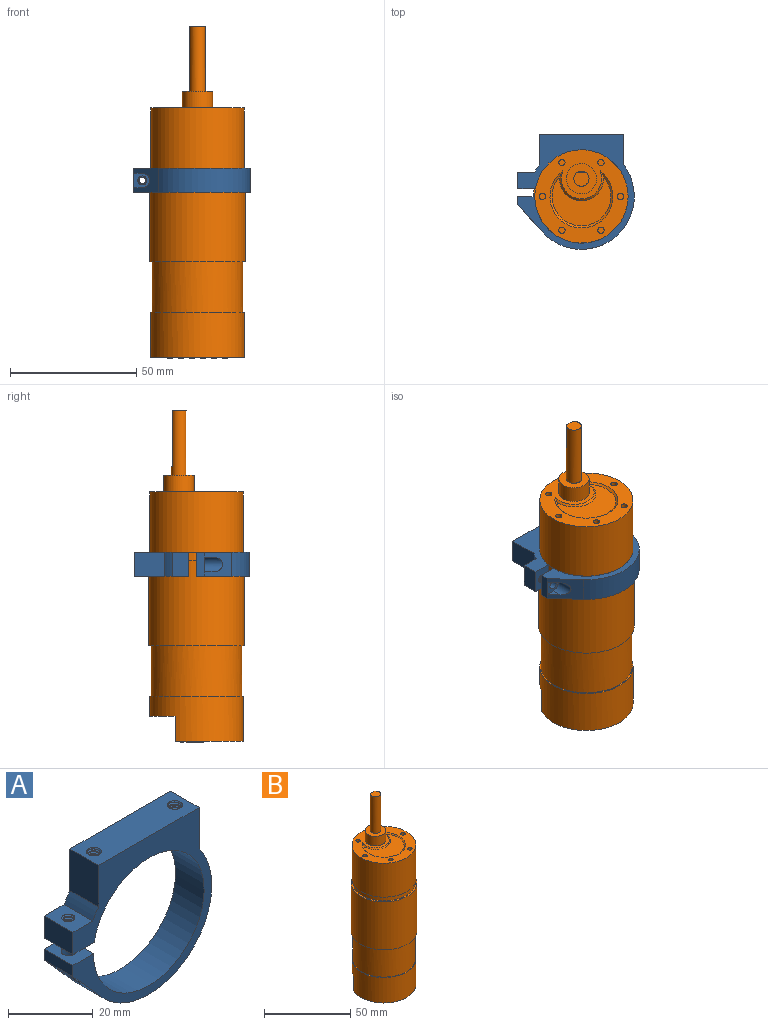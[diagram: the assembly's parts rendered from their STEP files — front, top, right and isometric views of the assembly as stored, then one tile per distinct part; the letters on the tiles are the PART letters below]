
ASSEMBLY  parts=2 mates=1
PART A: 53 faces, bbox 46.4x9.7x45.9 mm
  f0: cylinder r=1.75mm len=6.54mm, axis (0,0,-1), area 9mm2, adj f34,f50,f51,f52
  f1: cylinder r=1.75mm len=6.54mm, axis (0,0,-1), area 9mm2, adj f34,f47,f48,f49
  f2: cylinder r=1.75mm len=6.35mm, axis (0,0,1), area 8.7mm2, adj f30,f31,f45,f46
  f3: cylinder r=1.35mm len=6.35mm, axis (0,0,-1), area 15.8mm2, adj f30,f31,f45,f46
  f4: cylinder r=1.78mm len=3.56mm, axis (0,0,-1), area 35.5mm2, adj f38,f44
  f5: cylinder r=2.92mm len=7.1mm, axis (0,0,1), area 54.3mm2, adj f36,f42,f43,f44
  f6: cylinder r=1.35mm len=2.71mm, axis (0,0,1), area 7.6mm2, adj f7,f15,f47,f48,f49
  f7: cylinder r=1.35mm len=2.71mm, axis (0,0,1), area 2mm2, adj f6,f8,f48,f49
  f8: cylinder r=1.35mm len=2.71mm, axis (0,0,1), area 2mm2, adj f7,f9,f48,f49
  f9: cylinder r=1.35mm len=2.71mm, axis (0,0,1), area 2mm2, adj f8,f10,f48,f49
  f10: cylinder r=1.35mm len=2.71mm, axis (0,0,1), area 2mm2, adj f9,f11,f48,f49
  f11: cylinder r=1.35mm len=2.71mm, axis (0,0,1), area 2mm2, adj f10,f12,f48,f49
  f12: cylinder r=1.35mm len=2.71mm, axis (0,0,1), area 2mm2, adj f11,f13,f48,f49
  f13: cylinder r=1.35mm len=2.71mm, axis (0,0,1), area 2mm2, adj f12,f14,f48,f49
  f14: cylinder r=1.35mm len=2.71mm, axis (0,0,1), area 1.3mm2, adj f13,f28,f48,f49
  f15: cone r=1.35mm half-angle=59deg, axis (0,0,1), area 6.7mm2, adj f6
  f16: cylinder r=1.35mm len=2.71mm, axis (0,0,1), area 7.6mm2, adj f17,f25,f50,f51,f52
  f17: cylinder r=1.35mm len=2.71mm, axis (0,0,1), area 2mm2, adj f16,f18,f51,f52
  f18: cylinder r=1.35mm len=2.71mm, axis (0,0,1), area 2mm2, adj f17,f19,f51,f52
  f19: cylinder r=1.35mm len=2.71mm, axis (0,0,1), area 2mm2, adj f18,f20,f51,f52
  f20: cylinder r=1.35mm len=2.71mm, axis (0,0,1), area 2mm2, adj f19,f21,f51,f52
  f21: cylinder r=1.35mm len=2.71mm, axis (0,0,1), area 2mm2, adj f20,f22,f51,f52
  f22: cylinder r=1.35mm len=2.71mm, axis (0,0,1), area 2mm2, adj f21,f23,f51,f52
  f23: cylinder r=1.35mm len=2.71mm, axis (0,0,1), area 2mm2, adj f22,f24,f51,f52
  f24: cylinder r=1.35mm len=2.71mm, axis (0,0,1), area 1.3mm2, adj f23,f29,f51,f52
  f25: cone r=1.35mm half-angle=59deg, axis (0,0,1), area 6.7mm2, adj f16
  f26: cylinder r=18.41mm len=36.83mm, axis (0,-1,0), area 1071.7mm2, adj f30,f38,f40,f41
  f27: cylinder r=20.96mm len=36.58mm, axis (0,-1,0), area 610.3mm2, adj f35,f36,f40,f41
  f28: cone r=1.35mm half-angle=45deg, axis (0,0,1), area 3.3mm2, adj f14,f34,f48,f49
  f29: cone r=1.35mm half-angle=45deg, axis (0,0,1), area 3.3mm2, adj f24,f34,f51,f52
  f30: plane 9.72x7.33mm, normal (0,0,-1), area 60.6mm2, adj f2,f3,f26,f39,f40,f41,f45,f46
  f31: plane 9.72x6.8mm, normal (0,0,1), area 55.6mm2, adj f2,f3,f32,f39,f40,f41,f45,f46
  f32: cylinder r=20.96mm len=9.53mm, axis (0,-1,0), area 34.7mm2, adj f31,f33,f40,f41
  f33: plane 11.96x9.53mm, normal (-1,0,0), area 113.9mm2, adj f32,f34,f40,f41
  f34: plane 33.48x9.53mm, normal (0,0,1), area 299.6mm2, adj f0,f1,f28,f29,f33,f35,f40,f41
  f35: plane 11.96x9.53mm, normal (1,0,0), area 113.9mm2, adj f27,f34,f40,f41
  f36: plane 10.79x9.65mm, normal (-0.75,0,-0.67), area 87.8mm2, adj f5,f27,f37,f40,f41,f42,f43
  f37: plane 9.53x3.18mm, normal (-1,0,0), area 30.2mm2, adj f36,f38,f40,f41,f44
  f38: plane 9.53x6.86mm, normal (0,0,1), area 55.4mm2, adj f4,f26,f37,f40,f41
  f39: plane 9.53x6.35mm, normal (-1,0,0), area 60.5mm2, adj f30,f31,f40,f41
  f40: plane 46.23x45.52mm, normal (0,1,0), area 576.9mm2, adj f26,f27,f30,f31,f32,f33,f34,f35
  f41: plane 46.23x45.52mm, normal (0,-1,0), area 576.9mm2, adj f26,f27,f30,f31,f32,f33,f34,f35
  f42: plane 3.83x3.43mm, normal (0,-1,0), area 6.6mm2, adj f5,f36,f44
  f43: plane 3.83x3.43mm, normal (0,1,0), area 6.6mm2, adj f5,f36,f44
  f44: plane 6.35x5.84mm, normal (0,0,-1), area 23.5mm2, adj f4,f5,f37,f42,f43
  f45: bspline ~6.87x3.95mm, area 36.1mm2, adj f2,f3,f30,f31
  f46: bspline ~6.81x3.5mm, area 36.1mm2, adj f2,f3,f30,f31
  f47: cone r=0.98mm half-angle=55deg, axis (0,0,1), area 1.9mm2, adj f1,f6,f48,f49
  f48: bspline ~7.28x3.49mm, area 36.9mm2, adj f1,f6,f7,f8,f9,f10,f11,f12
  f49: bspline ~6.82x3.5mm, area 36.9mm2, adj f1,f6,f7,f8,f9,f10,f11,f12
  f50: cone r=0.98mm half-angle=55deg, axis (0,0,1), area 1.9mm2, adj f0,f16,f51,f52
  f51: bspline ~7.28x3.49mm, area 36.9mm2, adj f0,f16,f17,f18,f19,f20,f21,f22
  f52: bspline ~6.82x3.5mm, area 36.9mm2, adj f0,f16,f17,f18,f19,f20,f21,f22
PART B: 327 faces, bbox 38x38x131.7 mm
  f0: cone r=12.5mm half-angle=50deg, axis (0,0,1), area 63.4mm2, adj f1,f13,f284
  f1: cone r=8mm half-angle=45deg, axis (0,0,-1), area 30mm2, adj f0,f13,f284
  f2: plane 37x27mm, normal (0,0,-1), area 818.4mm2, adj f8,f14,f15,f16,f17,f18,f19,f20
  f3: plane 12x12mm, normal (0,0,1), area 84.8mm2, adj f10,f201
  f4: cylinder r=18.5mm len=37mm, axis (0,0,1), area 2789.7mm2, adj f253,f284
  f5: plane 0.87x0.8mm, normal (0,0,-1), area 0.5mm2, adj f32,f133,f223,f224
  f6: plane 0.87x0.8mm, normal (0,0,-1), area 0.5mm2, adj f244,f245,f246,f247
  f7: cylinder r=18mm len=36mm, axis (0,0,-1), area 2261.9mm2, adj f12,f70
  f8: cylinder r=18.5mm len=37mm, axis (0,0,-1), area 1687.7mm2, adj f2,f55,f70,f278
  f9: cylinder r=18mm len=36mm, axis (0,0,-1), area 339.3mm2, adj f11,f253
  f10: cylinder r=6mm len=12mm, axis (0,0,1), area 252.6mm2, adj f3,f284
  f11: plane 38x38mm, normal (0,0,1), area 116.2mm2, adj f9,f265
  f12: plane 38x38mm, normal (0,0,-1), area 116.2mm2, adj f7,f265
  f13: plane 23.33x19.48mm, normal (0,0,1), area 248.3mm2, adj f0,f1
  f14: plane 0.93x0.2mm, normal (-1,0,0), area 0.2mm2, adj f2,f152,f153,f216
  f15: bspline ~0.48x0.44mm, area 0.1mm2, adj f2,f130,f290,f324
  f16: bspline ~0.8x0.62mm, area 0.2mm2, adj f2,f203,f297,f300
  f17: plane 0.21x0.2mm, normal (0,-1,0), area 0mm2, adj f2,f72,f130,f316
  f18: bspline ~0.87x0.42mm, area 0.2mm2, adj f2,f75,f109,f256
  f19: plane 0.2x0.18mm, normal (1,0,0), area 0mm2, adj f2,f50,f206,f310
  f20: bspline ~0.71x0.33mm, area 0.2mm2, adj f2,f75,f256,f322
  f21: plane 0.2x0.18mm, normal (-1,0,0), area 0mm2, adj f2,f137,f205,f280
  f22: bspline ~0.61x0.56mm, area 0.2mm2, adj f2,f45,f130,f255
  f23: plane 1.57x1.32mm, normal (0.64,0.77,0), area 0.4mm2, adj f2,f98,f204,f280
  f24: bspline ~0.28x0.2mm, area 0.1mm2, adj f2,f105,f178,f179
  f25: plane 0.87x0.6mm, normal (0.57,-0.82,0), area 0.2mm2, adj f53,f200,f270,f279
  f26: plane 0.2x0.15mm, normal (0.73,-0.69,0), area 0mm2, adj f2,f132,f203,f319
  f27: plane 0.53x0.2mm, normal (0,-1,0), area 0.1mm2, adj f2,f96,f232,f325
  f28: bspline ~0.6x0.51mm, area 0.2mm2, adj f2,f58,f105,f184
  f29: bspline ~0.33x0.2mm, area 0.1mm2, adj f2,f60,f149,f303
  f30: bspline ~0.7x0.7mm, area 0.2mm2, adj f2,f104,f121,f294
  f31: plane 0.2x0.16mm, normal (0.79,-0.61,0), area 0mm2, adj f2,f40,f118,f191
  f32: bspline ~0.45x0.4mm, area 0.1mm2, adj f5,f133,f223,f326
  f33: plane 0.2x0.16mm, normal (0.79,-0.61,0), area 0mm2, adj f2,f225,f256,f262
  f34: plane 1.44x0.72mm, normal (0.45,0.89,0), area 0.3mm2, adj f2,f207,f208,f212
  f35: bspline ~0.83x0.35mm, area 0.2mm2, adj f2,f36,f37,f199
  f36: bspline ~0.87x0.42mm, area 0.2mm2, adj f2,f35,f196,f199
  f37: bspline ~0.71x0.25mm, area 0.2mm2, adj f2,f35,f39,f199
  f38: bspline ~0.87x0.42mm, area 0.2mm2, adj f2,f39,f198,f199
  f39: bspline ~1.08x1.04mm, area 0.3mm2, adj f2,f37,f38,f199
  f40: plane 2.1x1.95mm, normal (0,0,-1), area 1mm2, adj f31,f65,f118,f122,f125,f126,f191,f192
  f41: plane 1.44x0.72mm, normal (0.45,-0.89,0), area 0.3mm2, adj f2,f128,f208,f212
  f42: plane 0.23x0.2mm, normal (-1,0,0), area 0mm2, adj f129,f251,f254,f283
  f43: plane 0.2x0.03mm, normal (-1,0,0), area 0mm2, adj f2,f94,f160,f164
  f44: bspline ~0.63x0.2mm, area 0.1mm2, adj f2,f92,f283,f313
  f45: plane 0.2x0.18mm, normal (-1,0,0), area 0mm2, adj f2,f22,f130,f146
  f46: plane 0.37x0.2mm, normal (-1,0,0), area 0.1mm2, adj f2,f50,f95,f206
  f47: bspline ~0.61x0.61mm, area 0.2mm2, adj f2,f218,f219,f326
  f48: bspline ~0.59x0.59mm, area 0.2mm2, adj f2,f219,f220,f326
  f49: plane 2.5x2.5mm, normal (0,0,1), area 4.9mm2, adj f257
  f50: plane 2x0.2mm, normal (0,-1,0), area 0.4mm2, adj f2,f19,f46,f206
  f51: bspline ~0.43x0.41mm, area 0.1mm2, adj f2,f153,f214,f215
  f52: plane 1.36x0.2mm, normal (1,0,0), area 0.3mm2, adj f2,f90,f153,f216
  f53: plane 0.6x0.2mm, normal (-1,0,0), area 0.1mm2, adj f25,f200,f270,f279
  f54: plane 0.21x0.2mm, normal (0,1,0), area 0mm2, adj f2,f100,f147,f213
  f55: plane 32.86x10mm, normal (0,0,-1), area 234.6mm2, adj f8,f278
  f56: bspline ~0.2x0.17mm, area 0.1mm2, adj f2,f106,f271,f299
  f57: plane 2x0.27mm, normal (-0.13,-0.99,0), area 0.4mm2, adj f2,f135,f209,f212
  f58: bspline ~0.58x0.52mm, area 0.2mm2, adj f2,f28,f105,f183
  f59: bspline ~0.24x0.2mm, area 0mm2, adj f2,f104,f121,f304
  f60: plane 2.05x1.28mm, normal (0,0,-1), area 0.8mm2, adj f29,f82,f83,f85,f86,f87,f108,f142
  f61: plane 2x0.26mm, normal (-0.13,0.99,0), area 0.4mm2, adj f2,f79,f131,f212
  f62: plane 0.2x0.18mm, normal (1,0,0), area 0mm2, adj f2,f99,f153,f214
  f63: plane 0.62x0.2mm, normal (1,0,0), area 0.1mm2, adj f2,f103,f258,f283
  f64: bspline ~0.2x0.17mm, area 0.1mm2, adj f2,f233,f235,f236
  f65: plane 0.2x0.16mm, normal (-0.8,-0.6,0), area 0mm2, adj f2,f40,f125,f193
  f66: plane 0.31x0.2mm, normal (1,0,0), area 0.1mm2, adj f2,f95,f206,f310
  f67: plane 1.59x1.09mm, normal (-0.57,0.82,0), area 0.4mm2, adj f2,f143,f200,f291
  f68: bspline ~0.89x0.84mm, area 0.3mm2, adj f2,f203,f297,f319
  f69: plane 0.2x0.04mm, normal (-1,0,0), area 0mm2, adj f2,f145,f280,f315
  f70: plane 37x37mm, normal (0,0,1), area 57.3mm2, adj f7,f8
  f71: plane 1x0.21mm, normal (-0.2,0.98,0), area 0.2mm2, adj f2,f121,f287,f298
  f72: plane 0.82x0.2mm, normal (-1,0,0), area 0.2mm2, adj f2,f17,f130,f308
  f73: plane 2.1x1.23mm, normal (0,0,-1), area 0.8mm2, adj f127,f237,f238,f239,f240,f241,f242,f243
  f74: bspline ~0.51x0.42mm, area 0.1mm2, adj f2,f105,f177,f178
  f75: plane 0.2x0.16mm, normal (-0.8,-0.6,0), area 0mm2, adj f2,f18,f20,f256
  f76: bspline ~0.73x0.33mm, area 0.2mm2, adj f2,f148,f198,f199
  f77: plane 0.69x0.2mm, normal (0,1,0), area 0.1mm2, adj f2,f227,f232,f286
  f78: plane 0.2x0.18mm, normal (1,0,0), area 0mm2, adj f2,f159,f160,f164
  f79: plane 0.2x0.03mm, normal (-1,0,0), area 0mm2, adj f2,f61,f211,f212
  f80: plane 0.2x0.18mm, normal (1,0,0), area 0mm2, adj f2,f204,f280,f315
  f81: plane 0.53x0.2mm, normal (0.2,-0.98,0), area 0.1mm2, adj f2,f117,f130,f316
  f82: plane 2.05x0.2mm, normal (0,1,0), area 0.4mm2, adj f2,f60,f83,f86
  f83: plane 0.2x0.18mm, normal (1,0,0), area 0mm2, adj f2,f60,f82,f275
  f84: plane 2.1x1.95mm, normal (0,0,-1), area 1mm2, adj f91,f107,f120,f139,f141,f259,f261,f266
  f85: plane 0.87x0.2mm, normal (0,-1,0), area 0.2mm2, adj f2,f60,f86,f87
  f86: plane 0.2x0.18mm, normal (-1,0,0), area 0mm2, adj f2,f60,f82,f85
  f87: bspline ~0.56x0.3mm, area 0.1mm2, adj f2,f60,f85,f295
  f88: bspline ~0.71x0.33mm, area 0.2mm2, adj f2,f196,f197,f199
  f89: plane 0.2x0.03mm, normal (1,0,0), area 0mm2, adj f2,f185,f186,f190
  f90: plane 0.83x0.78mm, normal (-0.68,0.73,0), area 0.2mm2, adj f2,f52,f153,f215
  f91: bspline ~0.73x0.33mm, area 0.2mm2, adj f2,f84,f139,f281
  f92: bspline ~0.95x0.6mm, area 0.2mm2, adj f2,f44,f258,f283
  f93: bspline ~0.65x0.63mm, area 0.2mm2, adj f2,f117,f130,f255
  f94: plane 1.64x0.82mm, normal (-0.45,0.89,0), area 0.4mm2, adj f2,f43,f161,f164
  f95: plane 0.21x0.2mm, normal (-0.5,0.87,0), area 0mm2, adj f2,f46,f66,f206
  f96: plane 0.2x0.18mm, normal (1,0,0), area 0mm2, adj f2,f27,f97,f232
  f97: plane 2.05x0.2mm, normal (0,1,0), area 0.4mm2, adj f2,f96,f231,f232
  f98: plane 0.2x0.04mm, normal (1,0,0), area 0mm2, adj f2,f23,f205,f280
  f99: bspline ~0.67x0.65mm, area 0.2mm2, adj f2,f62,f151,f153
  f100: plane 0.77x0.2mm, normal (1,0,0), area 0.2mm2, adj f2,f54,f124,f147
  f101: plane 22.23x3.32mm, normal (0,1,0), area 73.7mm2, adj f201,f248,f289
  f102: plane 0.21x0.2mm, normal (0,1,0), area 0mm2, adj f2,f203,f296,f300
  f103: plane 2x0.2mm, normal (0,1,0), area 0.4mm2, adj f2,f63,f283,f313
  f104: bspline ~0.65x0.63mm, area 0.2mm2, adj f2,f30,f59,f121
  f105: plane 2.1x1.36mm, normal (0,0,-1), area 0.9mm2, adj f24,f28,f58,f74,f113,f114,f115,f175
  f106: bspline ~0.2x0.17mm, area 0.1mm2, adj f2,f56,f292,f299
  f107: bspline ~1.08x1.04mm, area 0.3mm2, adj f2,f84,f141,f259
  f108: bspline ~0.5x0.39mm, area 0.1mm2, adj f2,f60,f149,f264
  f109: bspline ~0.83x0.35mm, area 0.2mm2, adj f2,f18,f140,f256
  f110: bspline ~0.38x0.29mm, area 0.1mm2, adj f2,f232,f286,f293
  f111: plane 0.75x0.2mm, normal (0,-1,0), area 0.1mm2, adj f2,f227,f228,f232
  f112: plane 0.59x0.2mm, normal (0,1,0), area 0.1mm2, adj f2,f165,f173,f174
  f113: plane 0.21x0.2mm, normal (0,1,0), area 0mm2, adj f2,f105,f115,f177
  f114: bspline ~0.67x0.59mm, area 0.2mm2, adj f2,f105,f179,f180
  f115: bspline ~0.51x0.33mm, area 0.1mm2, adj f2,f105,f113,f176
  f116: plane 0.46x0.2mm, normal (0,1,0), area 0.1mm2, adj f2,f119,f200,f291
  f117: bspline ~0.24x0.2mm, area 0mm2, adj f2,f81,f93,f130
  f118: bspline ~0.73x0.33mm, area 0.2mm2, adj f2,f31,f40,f195
  f119: plane 0.2x0.18mm, normal (1,0,0), area 0mm2, adj f2,f116,f200,f306
  f120: plane 0.2x0.16mm, normal (-0.8,-0.6,0), area 0mm2, adj f2,f84,f266,f288
  f121: plane 2.05x1.31mm, normal (0,0,-1), area 0.9mm2, adj f30,f59,f71,f104,f202,f250,f252,f267
  f122: bspline ~0.83x0.35mm, area 0.2mm2, adj f2,f40,f192,f193
  f123: plane 0.23x0.2mm, normal (1,0,0), area 0mm2, adj f2,f144,f200,f306
  f124: plane 0.21x0.2mm, normal (0,-1,0), area 0mm2, adj f2,f100,f147,f213
  f125: bspline ~0.71x0.33mm, area 0.2mm2, adj f2,f40,f65,f194
  f126: bspline ~1.08x1.04mm, area 0.3mm2, adj f2,f40,f191,f192
  f127: plane 0.2x0.14mm, normal (-0.79,-0.62,0), area 0mm2, adj f2,f73,f237,f243
  f128: plane 1.44x0.2mm, normal (0.13,0.99,0), area 0.3mm2, adj f2,f41,f135,f212
  f129: bspline ~0.57x0.2mm, area 0.1mm2, adj f42,f251,f277,f283
  f130: plane 2.05x1.31mm, normal (0,0,-1), area 0.9mm2, adj f15,f17,f22,f45,f72,f81,f93,f117
  f131: plane 0.2x0.18mm, normal (1,0,0), area 0mm2, adj f2,f61,f207,f212
  f132: bspline ~0.9x0.39mm, area 0.2mm2, adj f2,f26,f203,f320
  f133: bspline ~0.44x0.4mm, area 0.1mm2, adj f5,f32,f224,f326
  f134: plane 0.59x0.2mm, normal (0,-1,0), area 0.1mm2, adj f2,f168,f169,f174
  f135: plane 0.2x0.18mm, normal (1,0,0), area 0mm2, adj f2,f57,f128,f212
  f136: plane 0.59x0.2mm, normal (0,1,0), area 0.1mm2, adj f2,f167,f168,f174
  f137: plane 1.57x0.2mm, normal (0,1,0), area 0.3mm2, adj f2,f21,f145,f280
  f138: plane 1.58x0.67mm, normal (-0.39,-0.92,0), area 0.3mm2, adj f2,f188,f189,f190
  f139: plane 0.2x0.16mm, normal (0.79,-0.61,0), area 0mm2, adj f2,f84,f91,f259
  f140: bspline ~0.71x0.25mm, area 0.2mm2, adj f2,f109,f226,f256
  f141: bspline ~0.71x0.25mm, area 0.2mm2, adj f2,f84,f107,f261
  f142: plane 0.75x0.2mm, normal (0,-1,0), area 0.1mm2, adj f2,f60,f269,f295
  f143: plane 0.2x0.04mm, normal (-1,0,0), area 0mm2, adj f2,f67,f200,f272
  f144: plane 0.21x0.2mm, normal (0,-1,0), area 0mm2, adj f2,f123,f200,f321
  f145: plane 1.57x1.32mm, normal (-0.64,-0.77,0), area 0.4mm2, adj f2,f69,f137,f280
  f146: bspline ~0.44x0.36mm, area 0.1mm2, adj f2,f45,f130,f290
  f147: plane 0.77x0.21mm, normal (0,0,-1), area 0.2mm2, adj f54,f100,f124,f213
  f148: bspline ~0.89x0.85mm, area 0.3mm2, adj f2,f76,f197,f199
  f149: bspline ~0.38x0.29mm, area 0.1mm2, adj f2,f29,f60,f108
  f150: bspline ~0.72x0.4mm, area 0.2mm2, adj f2,f151,f152,f153
  f151: bspline ~0.6x0.59mm, area 0.2mm2, adj f2,f99,f150,f153
  f152: plane 0.53x0.5mm, normal (0.68,-0.73,0), area 0.1mm2, adj f2,f14,f150,f153
  f153: plane 2.05x1.36mm, normal (0,0,-1), area 0.9mm2, adj f14,f51,f52,f62,f90,f99,f150,f151
  f154: plane 0.2x0.18mm, normal (1,0,0), area 0mm2, adj f2,f155,f163,f164
  f155: plane 1.44x0.2mm, normal (0.13,-0.99,0), area 0.3mm2, adj f2,f154,f156,f164
  f156: plane 1.44x0.72mm, normal (0.45,0.89,0), area 0.3mm2, adj f2,f155,f157,f164
  f157: plane 0.2x0.04mm, normal (1,0,0), area 0mm2, adj f2,f156,f158,f164
  f158: plane 1.44x0.72mm, normal (0.45,-0.89,0), area 0.3mm2, adj f2,f157,f159,f164
  f159: plane 1.44x0.2mm, normal (0.13,0.99,0), area 0.3mm2, adj f2,f78,f158,f164
  f160: plane 2x0.27mm, normal (-0.13,-0.99,0), area 0.4mm2, adj f2,f43,f78,f164
  f161: plane 1.64x0.83mm, normal (-0.45,-0.89,0), area 0.4mm2, adj f2,f94,f162,f164
  f162: plane 0.2x0.03mm, normal (-1,0,0), area 0mm2, adj f2,f161,f163,f164
  f163: plane 2x0.26mm, normal (-0.13,0.99,0), area 0.4mm2, adj f2,f154,f162,f164
  f164: plane 2.23x2mm, normal (0,0,-1), area 1.3mm2, adj f43,f78,f94,f154,f155,f156,f157,f158
  f165: plane 0.59x0.2mm, normal (-1,0,0), area 0.1mm2, adj f2,f112,f166,f174
  f166: plane 0.2x0.18mm, normal (0,1,0), area 0mm2, adj f2,f165,f167,f174
  f167: plane 0.59x0.2mm, normal (1,0,0), area 0.1mm2, adj f2,f136,f166,f174
  f168: plane 0.2x0.18mm, normal (1,0,0), area 0mm2, adj f2,f134,f136,f174
  f169: plane 0.59x0.2mm, normal (1,0,0), area 0.1mm2, adj f2,f134,f170,f174
  f170: plane 0.2x0.18mm, normal (0,-1,0), area 0mm2, adj f2,f169,f171,f174
  f171: plane 0.59x0.2mm, normal (-1,0,0), area 0.1mm2, adj f2,f170,f172,f174
  f172: plane 0.59x0.2mm, normal (0,-1,0), area 0.1mm2, adj f2,f171,f173,f174
  f173: plane 0.2x0.18mm, normal (-1,0,0), area 0mm2, adj f2,f112,f172,f174
  f174: plane 1.36x1.36mm, normal (0,0,-1), area 0.5mm2, adj f112,f134,f136,f165,f166,f167,f168,f169
  f175: bspline ~0.42x0.31mm, area 0.1mm2, adj f2,f105,f176,f184
  f176: bspline ~0.4x0.31mm, area 0.1mm2, adj f2,f105,f115,f175
  f177: bspline ~0.62x0.42mm, area 0.2mm2, adj f2,f74,f105,f113
  f178: bspline ~0.33x0.2mm, area 0.1mm2, adj f2,f24,f74,f105
  f179: plane 0.2x0.18mm, normal (-1,0,0), area 0mm2, adj f2,f24,f105,f114
  f180: bspline ~0.69x0.65mm, area 0.2mm2, adj f2,f105,f114,f181
  f181: bspline ~0.36x0.2mm, area 0.1mm2, adj f2,f105,f180,f182
  f182: bspline ~0.22x0.2mm, area 0.1mm2, adj f2,f105,f181,f183
  f183: bspline ~0.41x0.23mm, area 0.1mm2, adj f2,f58,f105,f182
  f184: plane 0.2x0.18mm, normal (1,0,0), area 0mm2, adj f2,f28,f105,f175
  f185: plane 2x0.85mm, normal (0.39,0.92,0), area 0.4mm2, adj f2,f89,f189,f190
  f186: plane 2x0.85mm, normal (0.39,-0.92,0), area 0.4mm2, adj f2,f89,f187,f190
  f187: plane 0.2x0.19mm, normal (-1,0,0), area 0mm2, adj f2,f186,f188,f190
  f188: plane 1.58x0.67mm, normal (-0.39,0.92,0), area 0.3mm2, adj f2,f138,f187,f190
  f189: plane 0.2x0.19mm, normal (-1,0,0), area 0mm2, adj f2,f138,f185,f190
  f190: plane 2x1.72mm, normal (0,0,-1), area 0.7mm2, adj f89,f138,f185,f186,f187,f188,f189
  f191: bspline ~0.87x0.42mm, area 0.2mm2, adj f2,f31,f40,f126
  f192: bspline ~0.71x0.25mm, area 0.2mm2, adj f2,f40,f122,f126
  f193: bspline ~0.87x0.42mm, area 0.2mm2, adj f2,f40,f65,f122
  f194: bspline ~0.9x0.84mm, area 0.3mm2, adj f2,f40,f125,f195
  f195: bspline ~0.89x0.85mm, area 0.3mm2, adj f2,f40,f118,f194
  f196: plane 0.2x0.16mm, normal (-0.8,-0.6,0), area 0mm2, adj f2,f36,f88,f199
  f197: bspline ~0.9x0.84mm, area 0.3mm2, adj f2,f88,f148,f199
  f198: plane 0.2x0.16mm, normal (0.79,-0.61,0), area 0mm2, adj f2,f38,f76,f199
  f199: plane 2.1x1.95mm, normal (0,0,-1), area 1mm2, adj f35,f36,f37,f38,f39,f76,f88,f148
  f200: plane 2.05x1.36mm, normal (0,0,-1), area 0.8mm2, adj f25,f53,f67,f116,f119,f123,f143,f144
  f201: cylinder r=3mm len=25.83mm, axis (0,0,1), area 408.7mm2, adj f3,f101,f248,f289
  f202: plane 0.2x0.18mm, normal (-1,0,0), area 0mm2, adj f2,f121,f294,f302
  f203: plane 2.1x2.1mm, normal (0,0,-1), area 1.2mm2, adj f16,f26,f68,f102,f132,f296,f297,f300
  f204: plane 1.57x0.2mm, normal (0,-1,0), area 0.3mm2, adj f2,f23,f80,f280
  f205: plane 2x0.2mm, normal (0,-1,0), area 0.4mm2, adj f2,f21,f98,f280
  f206: plane 2x0.49mm, normal (0,0,-1), area 0.4mm2, adj f19,f46,f50,f66,f95,f310
  f207: plane 1.44x0.2mm, normal (0.13,-0.99,0), area 0.3mm2, adj f2,f34,f131,f212
  f208: plane 0.2x0.04mm, normal (1,0,0), area 0mm2, adj f2,f34,f41,f212
  f209: plane 0.2x0.03mm, normal (-1,0,0), area 0mm2, adj f2,f57,f210,f212
  f210: plane 1.64x0.82mm, normal (-0.45,0.89,0), area 0.4mm2, adj f2,f209,f211,f212
  f211: plane 1.64x0.83mm, normal (-0.45,-0.89,0), area 0.4mm2, adj f2,f79,f210,f212
  f212: plane 2.23x2mm, normal (0,0,-1), area 1.3mm2, adj f34,f41,f57,f61,f79,f128,f131,f135
  f213: plane 0.77x0.2mm, normal (-1,0,0), area 0.2mm2, adj f2,f54,f124,f147
  f214: bspline ~0.46x0.46mm, area 0.1mm2, adj f2,f51,f62,f153
  f215: bspline ~0.61x0.38mm, area 0.1mm2, adj f2,f51,f90,f153
  f216: plane 0.21x0.2mm, normal (0,-1,0), area 0mm2, adj f2,f14,f52,f153
  f217: plane 0.91x0.6mm, normal (-0.55,0.84,0), area 0.2mm2, adj f2,f218,f222,f326
  f218: bspline ~0.58x0.22mm, area 0.1mm2, adj f2,f47,f217,f326
  f219: bspline ~0.63x0.61mm, area 0.2mm2, adj f2,f47,f48,f326
  f220: bspline ~0.21x0.2mm, area 0mm2, adj f2,f48,f221,f326
  f221: plane 0.81x0.53mm, normal (0.55,-0.84,0), area 0.2mm2, adj f2,f220,f222,f326
  f222: plane 0.2x0.14mm, normal (-0.79,-0.62,0), area 0mm2, adj f2,f217,f221,f326
  f223: bspline ~0.42x0.4mm, area 0.1mm2, adj f5,f32,f224,f326
  f224: bspline ~0.44x0.4mm, area 0.1mm2, adj f5,f133,f223,f326
  f225: bspline ~0.87x0.42mm, area 0.2mm2, adj f2,f33,f226,f256
  f226: bspline ~1.08x1.04mm, area 0.3mm2, adj f2,f140,f225,f256
  f227: plane 0.2x0.18mm, normal (1,0,0), area 0mm2, adj f2,f77,f111,f232
  f228: bspline ~0.74x0.55mm, area 0.2mm2, adj f2,f111,f229,f232
  f229: bspline ~0.56x0.3mm, area 0.1mm2, adj f2,f228,f230,f232
  f230: plane 0.87x0.2mm, normal (0,-1,0), area 0.2mm2, adj f2,f229,f231,f232
  f231: plane 0.2x0.18mm, normal (-1,0,0), area 0mm2, adj f2,f97,f230,f232
  f232: plane 2.05x1.28mm, normal (0,0,-1), area 0.8mm2, adj f27,f77,f96,f97,f110,f111,f227,f228
  f233: bspline ~0.2x0.17mm, area 0.1mm2, adj f2,f64,f234,f236
  f234: bspline ~0.2x0.17mm, area 0.1mm2, adj f2,f233,f235,f236
  f235: bspline ~0.2x0.17mm, area 0.1mm2, adj f2,f64,f234,f236
  f236: plane 0.33x0.33mm, normal (0,0,-1), area 0.1mm2, adj f64,f233,f234,f235
  f237: plane 0.91x0.6mm, normal (-0.55,0.84,0), area 0.2mm2, adj f2,f73,f127,f238
  f238: bspline ~0.58x0.22mm, area 0.1mm2, adj f2,f73,f237,f239
  f239: bspline ~0.61x0.61mm, area 0.2mm2, adj f2,f73,f238,f240
  f240: bspline ~0.63x0.61mm, area 0.2mm2, adj f2,f73,f239,f241
  f241: bspline ~0.59x0.59mm, area 0.2mm2, adj f2,f73,f240,f242
  f242: bspline ~0.21x0.2mm, area 0mm2, adj f2,f73,f241,f243
  f243: plane 0.81x0.53mm, normal (0.55,-0.84,0), area 0.2mm2, adj f2,f73,f127,f242
  f244: bspline ~0.45x0.4mm, area 0.1mm2, adj f6,f73,f245,f247
  f245: bspline ~0.42x0.4mm, area 0.1mm2, adj f6,f73,f244,f246
  f246: bspline ~0.44x0.4mm, area 0.1mm2, adj f6,f73,f245,f247
  f247: bspline ~0.44x0.4mm, area 0.1mm2, adj f6,f73,f244,f246
  f248: plane 6x5.5mm, normal (0,0,1), area 27.1mm2, adj f101,f201
  f249: cylinder r=1.25mm len=3.5mm, axis (0,0,-1), area 27.5mm2, adj f274,f284
  f250: plane 0.21x0.2mm, normal (0,-1,0), area 0mm2, adj f2,f121,f282,f287
  f251: plane 1.59x1.28mm, normal (0,0,-1), area 1.8mm2, adj f42,f129,f254,f260,f273,f276,f277
  f252: bspline ~0.48x0.44mm, area 0.1mm2, adj f2,f121,f267,f298
  f253: plane 37x37mm, normal (0,0,-1), area 57.3mm2, adj f4,f9
  f254: plane 1.59x0.2mm, normal (0,-1,0), area 0.3mm2, adj f42,f251,f273,f283
  f255: bspline ~0.7x0.7mm, area 0.2mm2, adj f2,f22,f93,f130
  f256: plane 2.1x1.95mm, normal (0,0,-1), area 1mm2, adj f18,f20,f33,f75,f109,f140,f225,f226
  f257: cylinder r=1.25mm len=3.5mm, axis (0,0,-1), area 27.5mm2, adj f49,f284
  f258: bspline ~1.02x0.97mm, area 0.3mm2, adj f2,f63,f92,f283
  f259: bspline ~0.87x0.42mm, area 0.2mm2, adj f2,f84,f107,f139
  f260: bspline ~0.61x0.2mm, area 0.1mm2, adj f251,f273,f276,f283
  f261: bspline ~0.83x0.35mm, area 0.2mm2, adj f2,f84,f141,f288
  f262: bspline ~0.73x0.33mm, area 0.2mm2, adj f2,f33,f256,f311
  f263: cylinder r=1.25mm len=3.5mm, axis (0,0,-1), area 27.5mm2, adj f268,f284
  f264: bspline ~0.39x0.2mm, area 0.1mm2, adj f2,f60,f108,f275
  f265: cylinder r=19mm len=38mm, axis (0,0,1), area 4058.9mm2, adj f11,f12
  f266: bspline ~0.71x0.33mm, area 0.2mm2, adj f2,f84,f120,f317
  f267: bspline ~0.51x0.51mm, area 0.2mm2, adj f2,f121,f252,f302
  f268: plane 2.5x2.5mm, normal (0,0,1), area 4.9mm2, adj f263
  f269: plane 0.2x0.18mm, normal (1,0,0), area 0mm2, adj f2,f60,f142,f303
  f270: plane 0.87x0.2mm, normal (0,1,0), area 0.2mm2, adj f25,f53,f200,f279
  f271: bspline ~0.2x0.17mm, area 0.1mm2, adj f2,f56,f292,f299
  f272: plane 1.38x0.2mm, normal (0,-1,0), area 0.3mm2, adj f2,f143,f200,f321
  f273: plane 0.2x0.14mm, normal (1,0,0), area 0mm2, adj f251,f254,f260,f283
  f274: plane 2.5x2.5mm, normal (0,0,1), area 4.9mm2, adj f249
  f275: plane 0.53x0.2mm, normal (0,-1,0), area 0.1mm2, adj f2,f60,f83,f264
  f276: bspline ~0.76x0.53mm, area 0.2mm2, adj f251,f260,f277,f283
  f277: bspline ~0.72x0.48mm, area 0.2mm2, adj f129,f251,f276,f283
  f278: plane 32.86x10mm, normal (0,1,0), area 328.6mm2, adj f2,f8,f55
  f279: plane 0.87x0.6mm, normal (0,0,-1), area 0.3mm2, adj f25,f53,f270
  f280: plane 2x1.54mm, normal (0,0,-1), area 1mm2, adj f21,f23,f69,f80,f98,f137,f145,f204
  f281: bspline ~0.89x0.85mm, area 0.3mm2, adj f2,f84,f91,f317
  f282: plane 0.68x0.2mm, normal (1,0,0), area 0.1mm2, adj f2,f121,f250,f304
  f283: plane 2x1.64mm, normal (0,0,-1), area 1.1mm2, adj f42,f44,f63,f92,f103,f129,f254,f258
  f284: plane 37x37mm, normal (0,0,1), area 614.7mm2, adj f0,f1,f4,f10,f249,f257,f263,f305
  f285: plane 2.5x2.5mm, normal (0,0,1), area 4.9mm2, adj f323
  f286: bspline ~0.33x0.2mm, area 0.1mm2, adj f2,f77,f110,f232
  f287: plane 0.82x0.2mm, normal (-1,0,0), area 0.2mm2, adj f2,f71,f121,f250
  f288: bspline ~0.87x0.42mm, area 0.2mm2, adj f2,f84,f120,f261
  f289: plane 3.32x0.5mm, normal (0,0,1), area 1.1mm2, adj f101,f201
  f290: bspline ~0.51x0.51mm, area 0.2mm2, adj f2,f15,f130,f146
  f291: plane 0.95x0.2mm, normal (1,0,0), area 0.2mm2, adj f2,f67,f116,f200
  f292: bspline ~0.2x0.17mm, area 0.1mm2, adj f2,f106,f271,f299
  f293: bspline ~0.5x0.39mm, area 0.1mm2, adj f2,f110,f232,f325
  f294: bspline ~0.61x0.56mm, area 0.2mm2, adj f2,f30,f121,f202
  f295: bspline ~0.74x0.55mm, area 0.2mm2, adj f2,f60,f87,f142
  f296: plane 0.85x0.2mm, normal (-1,0,0), area 0.2mm2, adj f2,f102,f203,f307
  f297: bspline ~0.95x0.86mm, area 0.3mm2, adj f2,f16,f68,f203
  f298: bspline ~0.44x0.2mm, area 0.1mm2, adj f2,f71,f121,f252
  f299: plane 0.33x0.33mm, normal (0,0,-1), area 0.1mm2, adj f56,f106,f271,f292
  f300: plane 0.67x0.2mm, normal (1,0,0), area 0.1mm2, adj f2,f16,f102,f203
  f301: plane 2.5x2.5mm, normal (0,0,1), area 4.9mm2, adj f314
  f302: bspline ~0.44x0.36mm, area 0.1mm2, adj f2,f121,f202,f267
  f303: plane 0.69x0.2mm, normal (0,1,0), area 0.1mm2, adj f2,f29,f60,f269
  f304: plane 0.53x0.2mm, normal (0.2,-0.98,0), area 0.1mm2, adj f2,f59,f121,f282
  f305: cylinder r=1.25mm len=3.5mm, axis (0,0,-1), area 27.5mm2, adj f284,f312
  f306: plane 0.46x0.2mm, normal (0,-1,0), area 0.1mm2, adj f2,f119,f123,f200
  f307: bspline ~1.03x0.99mm, area 0.3mm2, adj f2,f203,f296,f309
  f308: plane 1x0.21mm, normal (-0.2,0.98,0), area 0.2mm2, adj f2,f72,f130,f324
  f309: bspline ~0.87x0.38mm, area 0.2mm2, adj f2,f203,f307,f318
  f310: plane 1.8x0.2mm, normal (0,1,0), area 0.4mm2, adj f2,f19,f66,f206
  f311: bspline ~0.89x0.85mm, area 0.3mm2, adj f2,f256,f262,f322
  f312: plane 2.5x2.5mm, normal (0,0,1), area 4.9mm2, adj f305
  f313: plane 0.4x0.2mm, normal (-1,0,0), area 0.1mm2, adj f2,f44,f103,f283
  f314: cylinder r=1.25mm len=3.5mm, axis (0,0,-1), area 27.5mm2, adj f284,f301
  f315: plane 2x0.2mm, normal (0,1,0), area 0.4mm2, adj f2,f69,f80,f280
  f316: plane 0.68x0.2mm, normal (1,0,0), area 0.1mm2, adj f2,f17,f81,f130
  f317: bspline ~0.9x0.84mm, area 0.3mm2, adj f2,f84,f266,f281
  f318: bspline ~0.67x0.25mm, area 0.1mm2, adj f2,f203,f309,f320
  f319: bspline ~0.75x0.33mm, area 0.2mm2, adj f2,f26,f68,f203
  f320: bspline ~1.08x1.05mm, area 0.3mm2, adj f2,f132,f203,f318
  f321: plane 0.23x0.2mm, normal (-1,0,0), area 0mm2, adj f2,f144,f200,f272
  f322: bspline ~0.9x0.84mm, area 0.3mm2, adj f2,f20,f256,f311
  f323: cylinder r=1.25mm len=3.5mm, axis (0,0,-1), area 27.5mm2, adj f284,f285
  f324: bspline ~0.44x0.2mm, area 0.1mm2, adj f2,f15,f130,f308
  f325: bspline ~0.39x0.2mm, area 0.1mm2, adj f2,f27,f232,f293
  f326: plane 2.1x1.23mm, normal (0,0,-1), area 0.8mm2, adj f32,f47,f48,f133,f217,f218,f219,f220
PLACE A rot(axis=(-1,0,0),90deg) t=(-11.82,-0.68,16.43)mm
PLACE B t=(-11.82,-0.68,16.43)mm
MATE fastened A.f26 <-> B.f0  axis (0,0,1) through (-11.82,-0.68,16.43)mm
